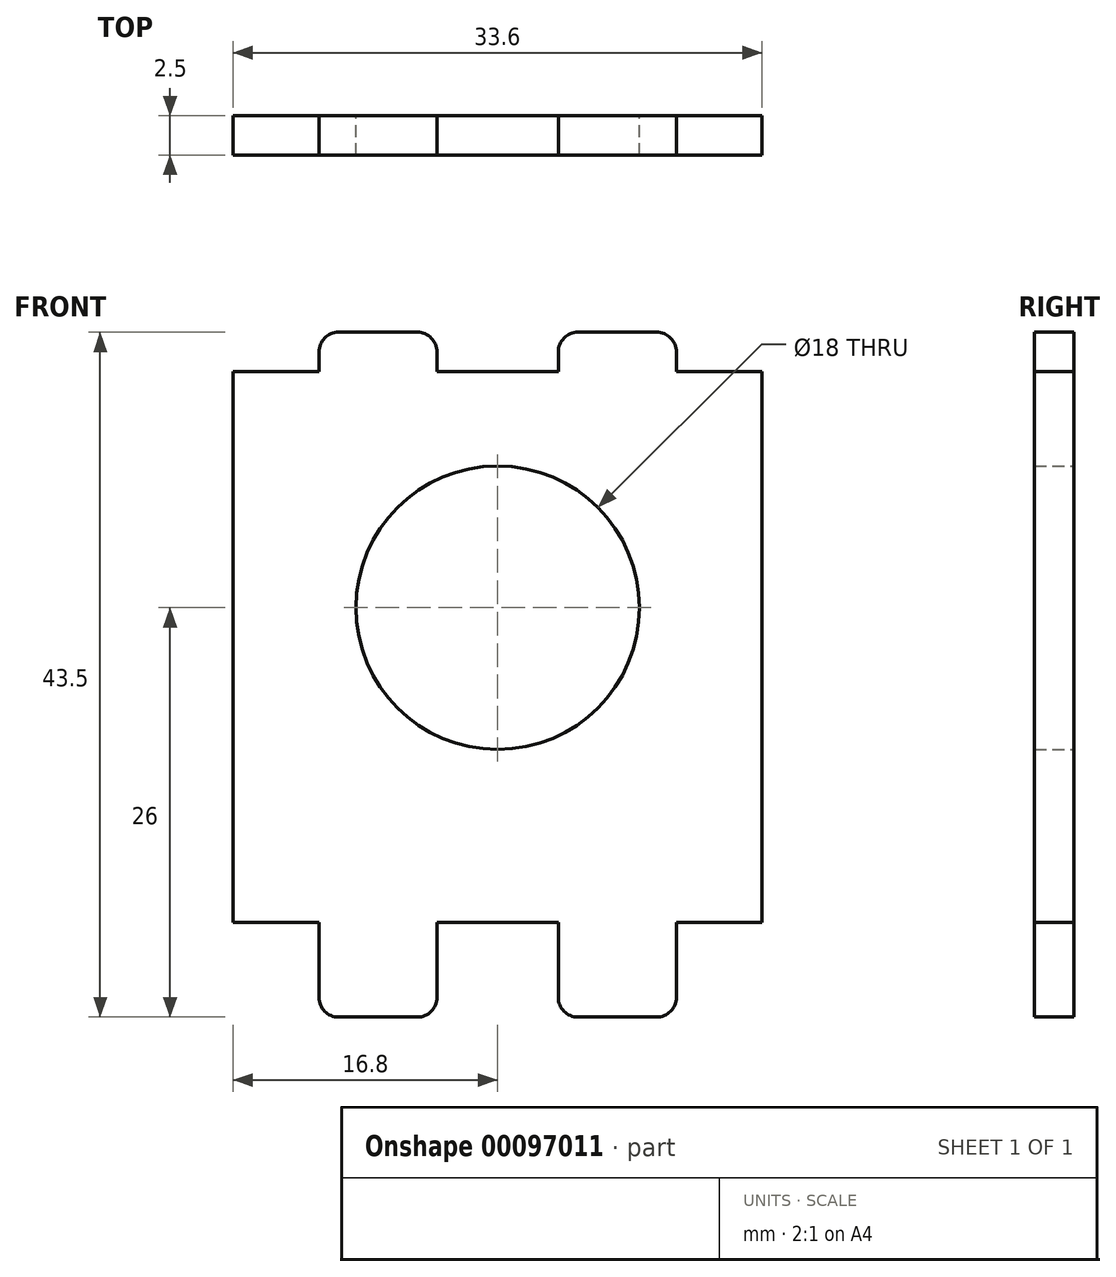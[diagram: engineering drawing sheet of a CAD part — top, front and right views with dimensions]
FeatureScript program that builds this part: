
annotation { "Feature Type Name" : "Feature", "Feature Type Description" : "" }
export const myFeature = defineFeature(function(context is Context, id is Id, definition is map)
    precondition{}
    {
        {
            var Q0;
            Q0=qCreatedBy(makeId("Front.planeOp"),FACE);
            var sketch = newSketch(context, id + "F0", { "sketchPlane" : qUnion([Q0])});
            skLineSegment(sketch, "E0.bottom", {"start": v(-16.8, 17.5) * mm, "end": v(-11.35, 17.5) * mm});
            skLineSegment(sketch, "E0.top", {"start": v(-16.8, -17.5) * mm, "end": v(-11.35, -17.5) * mm});
            skLineSegment(sketch, "E0.left", {"start": v(-16.8, 17.5) * mm, "end": v(-16.8, -17.5) * mm});
            skLineSegment(sketch, "E0.right", {"start": v(16.8, 17.5) * mm, "end": v(16.8, -17.5) * mm});
            skPoint(sketch, "E0.middle", {"position": v(0, 0) * mm});
            skLineSegment(sketch, "E1", {"start": v(-11.35, 18.75) * mm, "end": v(-11.35, 17.5) * mm});
            skLineSegment(sketch, "E2", {"start": v(11.35, 18.75) * mm, "end": v(11.35, 17.5) * mm});
            skLineSegment(sketch, "E3", {"start": v(-11.35, -17.5) * mm, "end": v(-11.35, -22.25) * mm});
            skLineSegment(sketch, "E4", {"start": v(11.35, -17.5) * mm, "end": v(11.35, -22.25) * mm});
            skLineSegment(sketch, "E5.trimOffspring", {"start": v(11.35, -17.5) * mm, "end": v(16.8, -17.5) * mm});
            skLineSegment(sketch, "E6.trimOffspring", {"start": v(11.35, 17.5) * mm, "end": v(16.8, 17.5) * mm});
            skLineSegment(sketch, "E7", {"start": v(-3.85, 17.5) * mm, "end": v(3.85, 17.5) * mm});
            skLineSegment(sketch, "E8", {"start": v(-3.85, -17.5) * mm, "end": v(3.85, -17.5) * mm});
            skLineSegment(sketch, "E9", {"start": v(-3.85, 18.75) * mm, "end": v(-3.85, 17.5) * mm});
            skLineSegment(sketch, "E10", {"start": v(3.85, 18.75) * mm, "end": v(3.85, 17.5) * mm});
            skPoint(sketch, "E10.endSnap0", {"position": v(0, 17.5) * mm});
            skLineSegment(sketch, "E11", {"start": v(-3.85, -17.5) * mm, "end": v(-3.85, -22.25) * mm});
            skLineSegment(sketch, "E12", {"start": v(3.85, -17.5) * mm, "end": v(3.85, -22.25) * mm});
            skPoint(sketch, "E13", {"position": v(-11.35, 18.75) * mm});
            skPoint(sketch, "E14", {"position": v(-3.85, 18.75) * mm});
            skPoint(sketch, "E15", {"position": v(3.85, 18.75) * mm});
            skPoint(sketch, "E16", {"position": v(11.35, 18.75) * mm});
            skPoint(sketch, "E17", {"position": v(11.35, -22.25) * mm});
            skPoint(sketch, "E18", {"position": v(3.85, -22.25) * mm});
            skPoint(sketch, "E19", {"position": v(-3.85, -22.25) * mm});
            skPoint(sketch, "E20", {"position": v(-11.35, -22.25) * mm});
            skPoint(sketch, "E21", {"position": v(-10.1, 20) * mm});
            skPoint(sketch, "E22", {"position": v(-5.1, 20) * mm});
            skPoint(sketch, "E23", {"position": v(5.1, 20) * mm});
            skPoint(sketch, "E24", {"position": v(10.1, 20) * mm});
            skPoint(sketch, "E25", {"position": v(-10.1, -23.5) * mm});
            skPoint(sketch, "E26", {"position": v(-5.1, -23.5) * mm});
            skPoint(sketch, "E27", {"position": v(5.1, -23.5) * mm});
            skPoint(sketch, "E28", {"position": v(10.1, -23.5) * mm});
            skLineSegment(sketch, "E29", {"start": v(-10.1, 20) * mm, "end": v(-5.1, 20) * mm});
            skLineSegment(sketch, "E30", {"start": v(5.1, 20) * mm, "end": v(10.1, 20) * mm});
            skLineSegment(sketch, "E31", {"start": v(-10.1, -23.5) * mm, "end": v(-5.1, -23.5) * mm});
            skLineSegment(sketch, "E32", {"start": v(5.1, -23.5) * mm, "end": v(10.1, -23.5) * mm});
            skArc(sketch, "E33", {"start": v(-10.1, 20) * mm, "mid": v(-10.98, 19.63) * mm, "end": v(-11.35, 18.75) * mm});
            skArc(sketch, "E34", {"start": v(-5.1, 20) * mm, "mid": v(-4.22, 19.63) * mm, "end": v(-3.85, 18.75) * mm});
            skArc(sketch, "E35", {"start": v(5.1, 20) * mm, "mid": v(4.22, 19.63) * mm, "end": v(3.85, 18.75) * mm});
            skArc(sketch, "E36", {"start": v(10.1, 20) * mm, "mid": v(10.98, 19.63) * mm, "end": v(11.35, 18.75) * mm});
            skArc(sketch, "E37", {"start": v(-10.1, -23.5) * mm, "mid": v(-10.98, -23.13) * mm, "end": v(-11.35, -22.25) * mm});
            skArc(sketch, "E38", {"start": v(-5.1, -23.5) * mm, "mid": v(-4.22, -23.13) * mm, "end": v(-3.85, -22.25) * mm});
            skArc(sketch, "E39", {"start": v(5.1, -23.5) * mm, "mid": v(4.22, -23.13) * mm, "end": v(3.85, -22.25) * mm});
            skArc(sketch, "E40", {"start": v(10.1, -23.5) * mm, "mid": v(10.98, -23.13) * mm, "end": v(11.35, -22.25) * mm});
            skLineSegment(sketch, "E41", {"start": v(-16.8, 2.5) * mm, "end": v(16.8, 2.5) * mm});
            skPoint(sketch, "E41.endSnap0", {"position": v(16.8, 0) * mm});
            skPoint(sketch, "E42", {"position": v(0, 2.5) * mm});
            skCircle(sketch, "E43", {"center": v(0, 2.5) * mm, "radius": 9 * mm});
            skSolve(sketch);
        }
        {
            var Q0;
            {var subQ1=sQuery(id+"F0.wireOp",EDGE,"E0.bottom");Q0=makeQuery(id+"F0.imprint","IMPRINT",FACE,{"disambiguationData":[TD([[makeQuery(id+"F0.imprint","IMPRINT",EDGE,{"derivedFrom":subQ1}),-1.0]])]});}
            var Q1;
            {var subQ7=sQuery(id+"F0.wireOp",EDGE,"E0.top");Q1=makeQuery(id+"F0.imprint","IMPRINT",FACE,{"disambiguationData":[TD([[makeQuery(id+"F0.imprint","IMPRINT",EDGE,{"derivedFrom":subQ7}),1.0]])]});}
            extrude(context, id + "F1", {"entities" : qUnion([Q0, Q1]), "depth" : 2.5 * mm});
        }
    });
